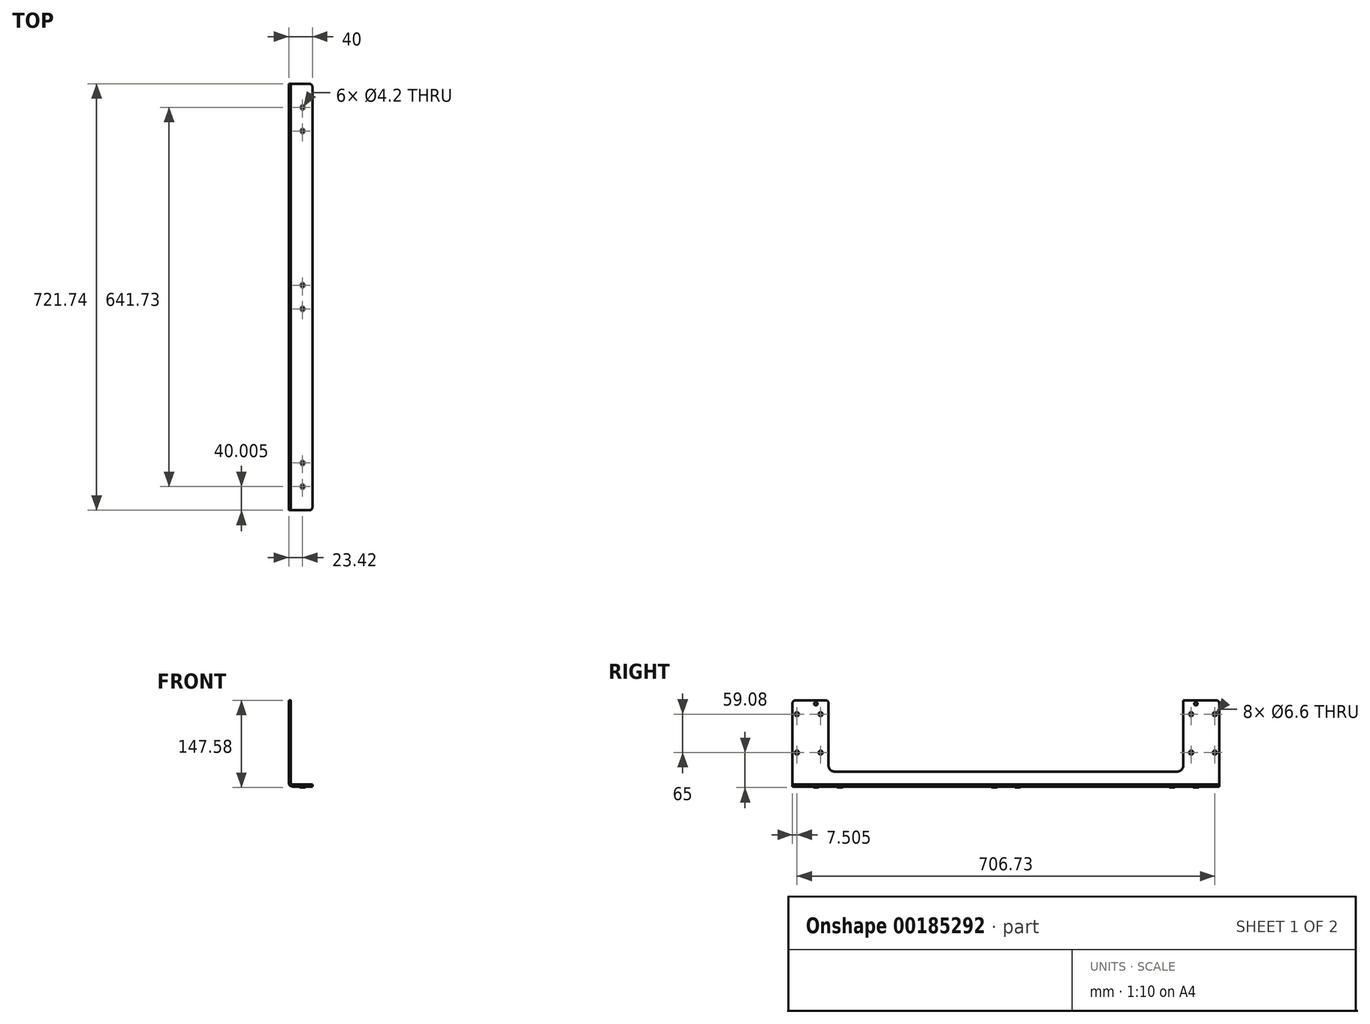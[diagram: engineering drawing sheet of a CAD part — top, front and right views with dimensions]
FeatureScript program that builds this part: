
annotation { "Feature Type Name" : "Feature", "Feature Type Description" : "" }
export const myFeature = defineFeature(function(context is Context, id is Id, definition is map)
    precondition{}
    {
        {
            var Q0;
            Q0=qCreatedBy(makeId("Front.planeOp"),FACE);
            var sketch = newSketch(context, id + "F0", { "sketchPlane" : qUnion([Q0])});
            skLineSegment(sketch, "E0.bottom", {"start": v(20, 73) * mm, "end": v(-20, 73) * mm, "construction": true});
            skLineSegment(sketch, "E0.top", {"start": v(20, -73) * mm, "end": v(-20, -73) * mm, "construction": true});
            skLineSegment(sketch, "E0.left", {"start": v(20, 73) * mm, "end": v(20, -73) * mm, "construction": true});
            skLineSegment(sketch, "E0.right", {"start": v(-20, 73) * mm, "end": v(-20, -73) * mm, "construction": true});
            skPoint(sketch, "E0.middle", {"position": v(0, 0) * mm});
            skLineSegment(sketch, "E1", {"start": v(-20, 73) * mm, "end": v(-16.58, 73) * mm});
            skLineSegment(sketch, "E2", {"start": v(-16.58, 73) * mm, "end": v(-16.58, -66.16) * mm});
            skLineSegment(sketch, "E3", {"start": v(-13.16, -69.58) * mm, "end": v(20, -69.58) * mm});
            skLineSegment(sketch, "E4", {"start": v(20, -69.58) * mm, "end": v(20, -73) * mm});
            skPoint(sketch, "E5.visualSharp", {"position": v(-16.58, -69.58) * mm});
            skArc(sketch, "E5.filletArc", {"start": v(-16.58, -66.16) * mm, "mid": v(-15.58, -68.58) * mm, "end": v(-13.16, -69.58) * mm});
            skLineSegment(sketch, "E6", {"start": v(20, -73) * mm, "end": v(-13.16, -73) * mm});
            skArc(sketch, "E7", {"start": v(-13.16, -73) * mm, "mid": v(-18, -71) * mm, "end": v(-20, -66.16) * mm});
            skLineSegment(sketch, "E8", {"start": v(-20, -66.16) * mm, "end": v(-20, 73) * mm});
            skSolve(sketch);
        }
        {
            var Q0;
            Q0 = qSketchRegion(id + "F0", true);
            extrude(context, id + "F1", {"entities" : qUnion([Q0]), "endBound" : BoundingType.SYMMETRIC, "depth" : 721.73 * mm});
        }
        {
            var Q0;
            Q0=makeQuery(id+"F1.opExtrude","SWEPT_FACE",FACE,{"disambiguationData":[OSD([sQuery(id+"F0.wireOp",EDGE,"E8")])]});
            var sketch = newSketch(context, id + "F2", { "sketchPlane" : qUnion([Q0])});
            skLineSegment(sketch, "E9.bottom", {"start": v(299.87, 73) * mm, "end": v(-299.87, 73) * mm});
            skLineSegment(sketch, "E9.top", {"start": v(299.87, -47.6) * mm, "end": v(-299.87, -47.6) * mm});
            skLineSegment(sketch, "E9.left", {"start": v(299.87, 73) * mm, "end": v(299.87, -47.6) * mm});
            skLineSegment(sketch, "E9.right", {"start": v(-299.87, 73) * mm, "end": v(-299.87, -47.6) * mm});
            skPoint(sketch, "E9.middle", {"position": v(0, 12.7) * mm});
            skSolve(sketch);
        }
        {
            var Q0;
            Q0 = qSketchRegion(id + "F2", true);
            extrude(context, id + "F3", {"entities" : qUnion([Q0]), "operationType" : NewBodyOperationType.REMOVE, "endBound" : BoundingType.THROUGH_ALL, "oppositeDirection" : true, "depth" : 25 * mm});
        }
        {
            var Q0;
            Q0=makeQuery(id+"F3.boolean.opBoolean","COPY",EDGE,{"derivedFrom":makeQuery(id+"F3.opExtrude","SWEPT_EDGE",EDGE,{"disambiguationData":[OSD([sQuery(id+"F2.wireOp",EDGE,"E9.top"),sQuery(id+"F2.wireOp",EDGE,"E9.right")])]})});
            var Q1;
            Q1=makeQuery(id+"F3.boolean.opBoolean","COPY",EDGE,{"derivedFrom":makeQuery(id+"F3.opExtrude","SWEPT_EDGE",EDGE,{"disambiguationData":[OSD([sQuery(id+"F2.wireOp",EDGE,"E9.top"),sQuery(id+"F2.wireOp",EDGE,"E9.left")])]})});
            fillet(context, id + "F4", {"entities" : qUnion([Q0, Q1]), "radius" : 10 * mm, "tangentPropagation" : true, "allowEdgeOverflow" : false});
        }
        {
            var Q0;
            Q0=makeQuery(id+"F1.opExtrude","CAP_EDGE",EDGE,{"disambiguationData":[OSD([sQuery(id+"F0.wireOp",EDGE,"E4")])],"isStart":false});
            var Q1;
            Q1=makeQuery(id+"F1.opExtrude","CAP_EDGE",EDGE,{"disambiguationData":[OSD([sQuery(id+"F0.wireOp",EDGE,"E4")])],"isStart":true});
            var Q2;
            Q2=makeQuery(id+"F1.opExtrude","CAP_EDGE",EDGE,{"disambiguationData":[OSD([sQuery(id+"F0.wireOp",EDGE,"E1")])],"isStart":false});
            var Q3;
            Q3=makeQuery(id+"F3.boolean.opBoolean","COPY",EDGE,{"derivedFrom":makeQuery(id+"F3.opExtrude","SWEPT_EDGE",EDGE,{"disambiguationData":[OSD([sQuery(id+"F0.wireOp",EDGE,"E1"),sQuery(id+"F0.wireOp",EDGE,"E8"),sQuery(id+"F2.wireOp",EDGE,"E9.bottom"),sQuery(id+"F2.wireOp",EDGE,"E9.left")])]})});
            var Q4;
            Q4=makeQuery(id+"F3.boolean.opBoolean","COPY",EDGE,{"derivedFrom":makeQuery(id+"F3.opExtrude","SWEPT_EDGE",EDGE,{"disambiguationData":[OSD([sQuery(id+"F0.wireOp",EDGE,"E1"),sQuery(id+"F0.wireOp",EDGE,"E8"),sQuery(id+"F2.wireOp",EDGE,"E9.bottom"),sQuery(id+"F2.wireOp",EDGE,"E9.right")])]})});
            var Q5;
            Q5=makeQuery(id+"F1.opExtrude","CAP_EDGE",EDGE,{"disambiguationData":[OSD([sQuery(id+"F0.wireOp",EDGE,"E1")])],"isStart":true});
            fillet(context, id + "F5", {"entities" : qUnion([Q0, Q1, Q2, Q3, Q4, Q5]), "radius" : 5 * mm, "tangentPropagation" : true, "allowEdgeOverflow" : false});
        }
        {
            var Q0;
            Q0=makeQuery(id+"F1.opExtrude","SWEPT_FACE",FACE,{"disambiguationData":[OSD([sQuery(id+"F0.wireOp",EDGE,"E8")])]});
            var sketch = newSketch(context, id + "F6", { "sketchPlane" : qUnion([Q0])});
            skPoint(sketch, "E10", {"position": v(-353.37, 49.5) * mm});
            skPoint(sketch, "E11", {"position": v(-313.37, 49.5) * mm});
            skPoint(sketch, "E12", {"position": v(-353.37, -15.5) * mm});
            skPoint(sketch, "E13", {"position": v(-313.37, -15.5) * mm});
            skPoint(sketch, "E14", {"position": v(313.36, -15.5) * mm});
            skPoint(sketch, "E15", {"position": v(353.37, -15.5) * mm});
            skPoint(sketch, "E16", {"position": v(353.37, 49.5) * mm});
            skPoint(sketch, "E17", {"position": v(313.37, 49.5) * mm});
            skLineSegment(sketch, "E18", {"start": v(-353.37, 49.5) * mm, "end": v(-353.37, -15.5) * mm, "construction": true});
            skLineSegment(sketch, "E19", {"start": v(-353.37, -15.5) * mm, "end": v(-313.37, -15.5) * mm, "construction": true});
            skLineSegment(sketch, "E20", {"start": v(-313.37, -15.5) * mm, "end": v(-313.37, 49.5) * mm, "construction": true});
            skLineSegment(sketch, "E21", {"start": v(-313.37, 49.5) * mm, "end": v(-353.37, 49.5) * mm, "construction": true});
            skLineSegment(sketch, "E22", {"start": v(313.37, 49.5) * mm, "end": v(353.37, 49.5) * mm, "construction": true});
            skLineSegment(sketch, "E23", {"start": v(353.37, 49.5) * mm, "end": v(353.37, -15.5) * mm, "construction": true});
            skLineSegment(sketch, "E24", {"start": v(313.37, 49.5) * mm, "end": v(313.37, -15.5) * mm, "construction": true});
            skLineSegment(sketch, "E25", {"start": v(313.36, -15.5) * mm, "end": v(353.37, -15.5) * mm, "construction": true});
            skSolve(sketch);
        }
        {
            var Q0;
            Q0=sQuery(id+"F6.wireOp",VERTEX,"E13");
            var Q1;
            Q1=sQuery(id+"F6.wireOp",VERTEX,"E12");
            var Q2;
            Q2=sQuery(id+"F6.wireOp",VERTEX,"E11");
            var Q3;
            Q3=sQuery(id+"F6.wireOp",VERTEX,"E10");
            var Q4;
            Q4=sQuery(id+"F6.wireOp",VERTEX,"E17");
            var Q5;
            Q5=sQuery(id+"F6.wireOp",VERTEX,"E16");
            var Q6;
            Q6=sQuery(id+"F6.wireOp",VERTEX,"E15");
            var Q7;
            Q7=sQuery(id+"F6.wireOp",VERTEX,"E14");
            var Q8;
            Q8=makeQuery(id+"F1.opExtrude","SWEPT_BODY",BODY,{"disambiguationData":[OSD([sQuery(id+"F0.wireOp",EDGE,"E1"),sQuery(id+"F0.wireOp",EDGE,"E2"),sQuery(id+"F0.wireOp",EDGE,"E3"),sQuery(id+"F0.wireOp",EDGE,"E4"),sQuery(id+"F0.wireOp",EDGE,"E5.filletArc"),sQuery(id+"F0.wireOp",EDGE,"E6"),sQuery(id+"F0.wireOp",EDGE,"E7"),sQuery(id+"F0.wireOp",EDGE,"E8")])]});
            hole(context, id + "F7", {"style" : HoleStyle.SIMPLE, "endStyle" : HoleEndStyle.THROUGH, "standardTappedOrClearance" : lookupTablePath({ "standard" : "ISO", "fit" : "Normal", "size" : "M6", "type" : "Clearance" }), "standardBlindInLast" : lookupTablePath({ "fit" : "Standard", "standard" : "ISO", "size" : "M6", "type" : "Clearance" }), "holeDiameter" : 6.6 * mm, "locations" : qUnion([Q0, Q1, Q2, Q3, Q4, Q5, Q6, Q7]), "scope" : qUnion([Q8]), "isTappedThrough" : true});
        }
        {
            var Q0;
            Q0=makeQuery(id+"F1.opExtrude","SWEPT_FACE",FACE,{"disambiguationData":[OSD([sQuery(id+"F0.wireOp",EDGE,"E3")])]});
            var sketch = newSketch(context, id + "F8", { "sketchPlane" : qUnion([Q0])});
            skLineSegment(sketch, "E26", {"start": v(3.42, 320.87) * mm, "end": v(3.42, 20) * mm, "construction": true});
            skLineSegment(sketch, "E27", {"start": v(3.42, 20) * mm, "end": v(3.42, -20) * mm, "construction": true});
            skLineSegment(sketch, "E28", {"start": v(3.42, -20) * mm, "end": v(3.42, -320.87) * mm, "construction": true});
            skLineSegment(sketch, "E29", {"start": v(0, 0) * mm, "end": v(3.42, 0) * mm, "construction": true});
            skCircle(sketch, "E30", {"center": v(3.42, 320.87) * mm, "radius": 4.5 * mm});
            skCircle(sketch, "E31", {"center": v(3.42, 20) * mm, "radius": 4.5 * mm});
            skCircle(sketch, "E32", {"center": v(3.42, -20) * mm, "radius": 4.5 * mm});
            skCircle(sketch, "E33", {"center": v(3.42, -320.87) * mm, "radius": 4.5 * mm});
            skCircle(sketch, "E34", {"center": v(3.42, -280.87) * mm, "radius": 4.5 * mm});
            skCircle(sketch, "E35", {"center": v(3.42, 280.87) * mm, "radius": 4.5 * mm});
            skSolve(sketch);
        }
        {
            var Q0;
            Q0 = qSketchRegion(id + "F8", true);
            extrude(context, id + "F9", {"entities" : qUnion([Q0]), "operationType" : NewBodyOperationType.ADD, "oppositeDirection" : true, "depth" : 5 * mm});
        }
        {
            var Q0;
            Q0=sQuery(id+"F8.wireOp",VERTEX,"E28.end");
            var Q1;
            Q1=sQuery(id+"F8.wireOp",VERTEX,"E28.start");
            var Q2;
            Q2=sQuery(id+"F8.wireOp",VERTEX,"E27.start");
            var Q3;
            Q3=sQuery(id+"F8.wireOp",VERTEX,"E30.center");
            var Q4;
            Q4=sQuery(id+"F8.wireOp",VERTEX,"E35.center");
            var Q5;
            Q5=sQuery(id+"F8.wireOp",VERTEX,"E34.center");
            var Q6;
            Q6=makeQuery(id+"F1.opExtrude","SWEPT_BODY",BODY,{"disambiguationData":[OSD([sQuery(id+"F0.wireOp",EDGE,"E1"),sQuery(id+"F0.wireOp",EDGE,"E2"),sQuery(id+"F0.wireOp",EDGE,"E3"),sQuery(id+"F0.wireOp",EDGE,"E4"),sQuery(id+"F0.wireOp",EDGE,"E5.filletArc"),sQuery(id+"F0.wireOp",EDGE,"E6"),sQuery(id+"F0.wireOp",EDGE,"E7"),sQuery(id+"F0.wireOp",EDGE,"E8")])]});
            hole(context, id + "F10", {"style" : HoleStyle.SIMPLE, "endStyle" : HoleEndStyle.THROUGH, "standardTappedOrClearance" : lookupTablePath({ "standard" : "ISO", "engagement" : "75%", "pitch" : "0.8 mm", "size" : "M5", "type" : "Tapped" }), "standardBlindInLast" : lookupTablePath({ "standard" : "ISO", "engagement" : "75%", "pitch" : "0.8 mm", "size" : "M5", "type" : "Tapped" }), "holeDiameter" : 4.2 * mm, "locations" : qUnion([Q0, Q1, Q2, Q3, Q4, Q5]), "scope" : qUnion([Q6]), "isTappedThrough" : true, "majorDiameter" : 5 * mm, "showTappedDepth" : true});
        }
        {
            var Q0;
            Q0=makeQuery(id+"F1.opExtrude","SWEPT_FACE",FACE,{"disambiguationData":[OSD([sQuery(id+"F0.wireOp",EDGE,"E8")])]});
            var sketch = newSketch(context, id + "F11", { "sketchPlane" : qUnion([Q0])});
            skLineSegment(sketch, "E36.bottom", {"start": v(321.37, 70) * mm, "end": v(-321.37, 70) * mm, "construction": true});
            skLineSegment(sketch, "E36.top", {"start": v(321.37, 64) * mm, "end": v(-321.37, 64) * mm, "construction": true});
            skLineSegment(sketch, "E36.left", {"start": v(321.37, 70) * mm, "end": v(321.37, 64) * mm, "construction": true});
            skLineSegment(sketch, "E36.right", {"start": v(-321.37, 70) * mm, "end": v(-321.37, 64) * mm, "construction": true});
            skPoint(sketch, "E36.middle", {"position": v(0, 67) * mm});
            skPoint(sketch, "E37", {"position": v(321.37, 67) * mm});
            skPoint(sketch, "E38", {"position": v(-321.37, 67) * mm});
            skSolve(sketch);
        }
        {
            var Q0;
            Q0=sQuery(id+"F11.wireOp",VERTEX,"E38");
            var Q1;
            Q1=sQuery(id+"F11.wireOp",VERTEX,"E37");
            var Q2;
            Q2=makeQuery(id+"F1.opExtrude","SWEPT_BODY",BODY,{"disambiguationData":[OSD([sQuery(id+"F0.wireOp",EDGE,"E1"),sQuery(id+"F0.wireOp",EDGE,"E2"),sQuery(id+"F0.wireOp",EDGE,"E3"),sQuery(id+"F0.wireOp",EDGE,"E4"),sQuery(id+"F0.wireOp",EDGE,"E5.filletArc"),sQuery(id+"F0.wireOp",EDGE,"E6"),sQuery(id+"F0.wireOp",EDGE,"E7"),sQuery(id+"F0.wireOp",EDGE,"E8")])]});
            hole(context, id + "F12", {"style" : HoleStyle.SIMPLE, "endStyle" : HoleEndStyle.THROUGH, "standardTappedOrClearance" : lookupTablePath({ "standard" : "ISO", "fit" : "Normal", "size" : "M5", "type" : "Clearance" }), "standardBlindInLast" : lookupTablePath({ "fit" : "Standard", "standard" : "ISO", "size" : "M5", "type" : "Clearance" }), "holeDiameter" : 5.5 * mm, "locations" : qUnion([Q0, Q1]), "scope" : qUnion([Q2]), "isTappedThrough" : true});
        }
    });
